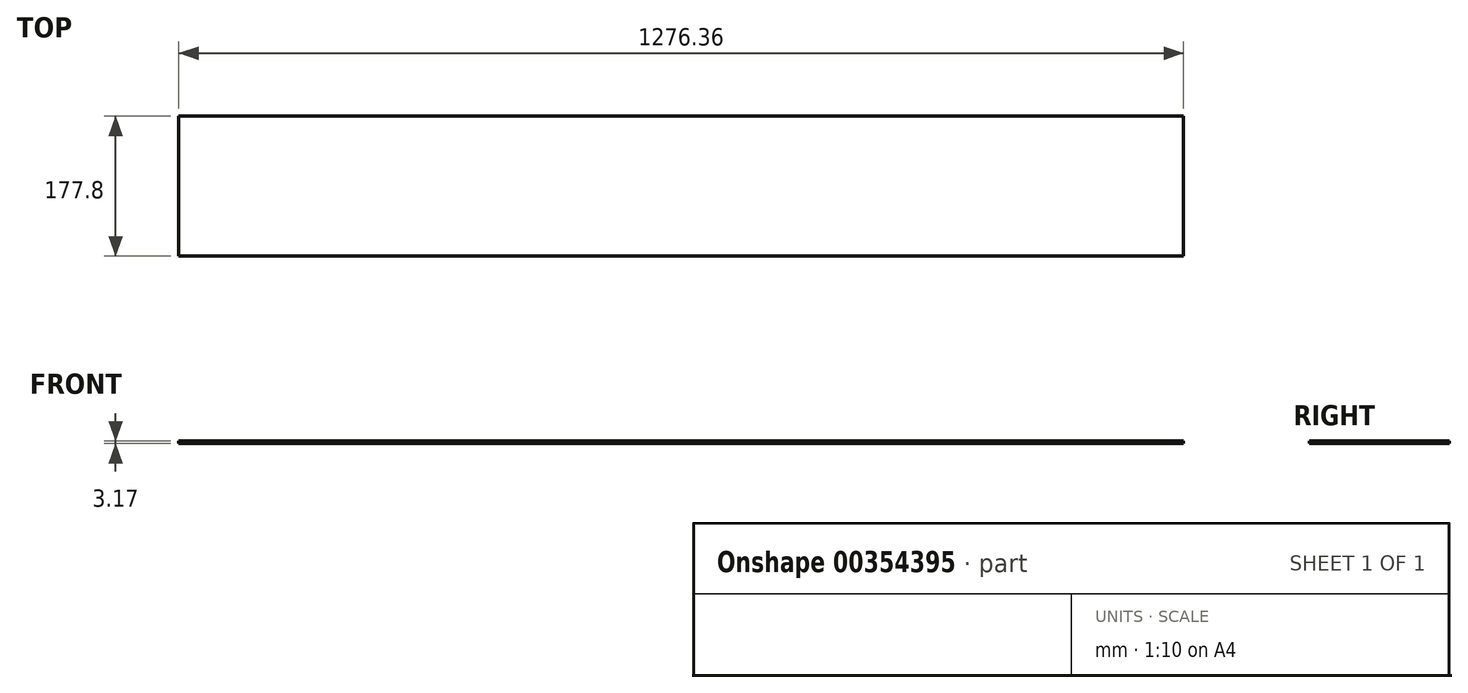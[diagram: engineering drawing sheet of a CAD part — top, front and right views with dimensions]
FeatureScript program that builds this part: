
annotation { "Feature Type Name" : "Feature", "Feature Type Description" : "" }
export const myFeature = defineFeature(function(context is Context, id is Id, definition is map)
    precondition{}
    {
        {
            var Q0;
            Q0=qCreatedBy(makeId("Top.planeOp"),FACE);
            var sketch = newSketch(context, id + "F0", { "sketchPlane" : qUnion([Q0])});
            skLineSegment(sketch, "E0.bottom", {"start": v(-638.18, 88.9) * mm, "end": v(638.17, 88.9) * mm});
            skLineSegment(sketch, "E0.top", {"start": v(-638.18, -88.9) * mm, "end": v(638.18, -88.9) * mm});
            skLineSegment(sketch, "E0.left", {"start": v(-638.18, 88.9) * mm, "end": v(-638.18, -88.9) * mm});
            skLineSegment(sketch, "E0.right", {"start": v(638.18, 88.9) * mm, "end": v(638.18, -88.9) * mm});
            skPoint(sketch, "E0.middle", {"position": v(0, 0) * mm});
            skSolve(sketch);
        }
        {
            var Q0;
            Q0 = qSketchRegion(id + "F0", true);
            extrude(context, id + "F1", {"entities" : qUnion([Q0]), "depth" : 3.17 * mm});
        }
    });
